# Revit family: TV203-C-1.9
name_source: partatom
category: Aparatos sanitarios
units: mm (PartAtom-declared; Revit-internal decimal feet)

## family parameters
Compartido = No
Corte con vacíos al cargar = No
Cota de conector redondo = Diámetro de uso
Número OmniClass = 23.45.00.00
Punto de cálculo de habitación = No
Se basa en plano de trabajo = No
Siempre vertical = Sí
Tipo de pieza = Normal
Título OmniClass = Sanitary, Laundry, and Cleaning Equipment

## types (1)
- TV203-C-1.9
    Accesorios = Llave allen 2mm, Llave para aireador, Kit de sujeción, Módulo electrónico
    Chrome = Brass Chromed
    Comentarios de tipo = Línea Electrónica
    Conexión AF = No
    Descripción = Llave de Lavabo Electrónica de Sensor de Corriente a Pared
    Detection Range = 9.8" (25 cm)
    Electrónico = Sensor infrarrojo, Distancia de detección 25cm (ajuste de fábrica), Fuente de alimentación regulada clase 2, Entrada: 115 - 230 Vca, 50/60 Hz, Salida: 6V cc/200mA
    Elevación por defecto = 0"
    Fabricante = HELVEX
    Feeding Voltage = 6 V
    Inlet Threads = ½" - 14 NPSM
    Max. Working Pressure = 85.3 psi
    Min. Working Pressure = 8.5 psi
    Modelo = TV203-C-1.9
    Operación = Active la salida colocando su mano dentro de la
zona de detección.
    Support Base Diameter = 3"
    Total Height = 14"
    Total Length = 6"

## geometry (parser evidence)
native form markers: Sweep x3
no freeform markers — native parametric forms only
